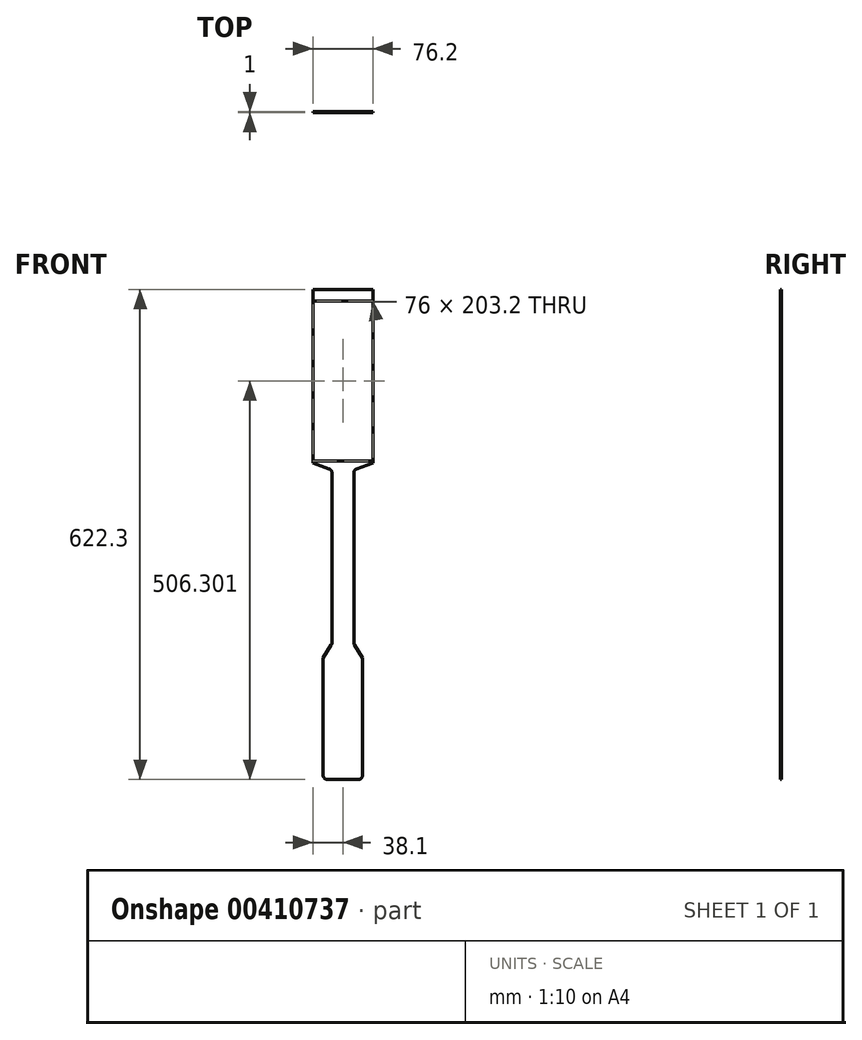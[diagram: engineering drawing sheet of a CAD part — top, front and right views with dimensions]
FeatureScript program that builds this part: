
annotation { "Feature Type Name" : "Feature", "Feature Type Description" : "" }
export const myFeature = defineFeature(function(context is Context, id is Id, definition is map)
    precondition{}
    {
        {
            var Q0;
            Q0=qCreatedBy(makeId("Front.planeOp"),FACE);
            var sketch = newSketch(context, id + "F0", { "sketchPlane" : qUnion([Q0])});
            skLineSegment(sketch, "E0.bottom", {"start": v(-38.1, 220.64) * mm, "end": v(0, 220.64) * mm});
            skLineSegment(sketch, "E0.left", {"start": v(-38.1, 220.64) * mm, "end": v(-38.1, 0) * mm});
            skLineSegment(sketch, "E1", {"start": v(0, 0) * mm, "end": v(0, 323.16) * mm, "construction": true});
            skLineSegment(sketch, "E2", {"start": v(-38.1, 0) * mm, "end": v(-17.34, -7.28) * mm});
            skLineSegment(sketch, "E3", {"start": v(-14, -12) * mm, "end": v(-14, -228.48) * mm});
            skLineSegment(sketch, "E4", {"start": v(-14.77, -231.15) * mm, "end": v(-25, -247.36) * mm});
            skLineSegment(sketch, "E5", {"start": v(-25, -247.36) * mm, "end": v(-25, -396.66) * mm});
            skLineSegment(sketch, "E6", {"start": v(-20, -401.66) * mm, "end": v(0, -401.66) * mm});
            skLineSegment(sketch, "E7", {"start": v(0, 206.24) * mm, "end": v(-38, 206.24) * mm});
            skLineSegment(sketch, "E8", {"start": v(-38, 206.24) * mm, "end": v(-38, 3.04) * mm});
            skLineSegment(sketch, "E9", {"start": v(-38, 3.04) * mm, "end": v(0, 3.04) * mm});
            skLineSegment(sketch, "E10.MirrorCS", {"start": v(0, 206.24) * mm, "end": v(38, 206.24) * mm});
            skLineSegment(sketch, "E11.MirrorCS", {"start": v(38.1, 220.64) * mm, "end": v(0, 220.64) * mm});
            skLineSegment(sketch, "E12.MirrorCS", {"start": v(38.1, 220.64) * mm, "end": v(38.1, 0) * mm});
            skLineSegment(sketch, "E13.MirrorCS", {"start": v(38, 206.24) * mm, "end": v(38, 3.04) * mm});
            skLineSegment(sketch, "E14.MirrorCS", {"start": v(38, 3.04) * mm, "end": v(0, 3.04) * mm});
            skLineSegment(sketch, "E15.MirrorCS", {"start": v(38.1, 0) * mm, "end": v(17.34, -7.28) * mm});
            skLineSegment(sketch, "E16.MirrorCS", {"start": v(14, -12) * mm, "end": v(14, -228.48) * mm});
            skLineSegment(sketch, "E17.MirrorCS", {"start": v(14.77, -231.15) * mm, "end": v(25, -247.36) * mm});
            skLineSegment(sketch, "E18.MirrorCS", {"start": v(25, -247.36) * mm, "end": v(25, -396.66) * mm});
            skLineSegment(sketch, "E19.MirrorCS", {"start": v(20, -401.66) * mm, "end": v(0, -401.66) * mm});
            skPoint(sketch, "E20.visualSharp", {"position": v(-14, -8.46) * mm});
            skArc(sketch, "E20.filletArc", {"start": v(-14, -12) * mm, "mid": v(-14.92, -9.1) * mm, "end": v(-17.34, -7.28) * mm});
            skPoint(sketch, "E21.visualSharp", {"position": v(14, -8.46) * mm});
            skArc(sketch, "E21.filletArc", {"start": v(17.34, -7.28) * mm, "mid": v(14.92, -9.1) * mm, "end": v(14, -12) * mm});
            skPoint(sketch, "E22.visualSharp", {"position": v(-14, -229.93) * mm});
            skArc(sketch, "E22.filletArc", {"start": v(-14.77, -231.15) * mm, "mid": v(-14.2, -229.87) * mm, "end": v(-14, -228.48) * mm});
            skPoint(sketch, "E23.visualSharp", {"position": v(14, -229.93) * mm});
            skArc(sketch, "E23.filletArc", {"start": v(14, -228.48) * mm, "mid": v(14.2, -229.87) * mm, "end": v(14.77, -231.15) * mm});
            skPoint(sketch, "E24.visualSharp", {"position": v(-25, -401.66) * mm});
            skArc(sketch, "E24.filletArc", {"start": v(-25, -396.66) * mm, "mid": v(-23.54, -400.2) * mm, "end": v(-20, -401.66) * mm});
            skPoint(sketch, "E25.visualSharp", {"position": v(25, -401.66) * mm});
            skArc(sketch, "E25.filletArc", {"start": v(20, -401.66) * mm, "mid": v(23.54, -400.2) * mm, "end": v(25, -396.66) * mm});
            skSolve(sketch);
        }
        {
            var Q0;
            Q0 = qSketchRegion(id + "F0", true);
            extrude(context, id + "F1", {"entities" : qUnion([Q0]), "depth" : 1 * mm});
        }
    });
